# Revit family: Gira_207705
name_source: partatom
category: Electrical Fixtures
revit_build: Autodesk Revit 2017 (Build: 20160225_1515(x64)
units: mm (PartAtom-declared; Revit-internal decimal feet)

## family parameters
Cut with Voids When Loaded = No
Host = Face
Maintain Annotation Orientation = Yes
Part Type = Normal
Room Calculation Point = No
Round Connector Dimension = Use Diameter
Shared = No

## types (1)
- Gira G1 24 V Gira G1 black gl.
    BIM = https://media.live.bim.site
    BIMSITE_PRODUCT_ID = 3473432342bc8b360301786b060e44153b5fdd08
    Bus connection included = No
    Central functional unit for senders/actuators = Yes
    Colour = Black
    Cost = 0 $
    Default Elevation = 1219 mm
    Description = Gira G1 24V G1 GBk Gira G1 24 V,black glass The Gira G1 is a multi-functional room operating device for visualising and operating a variety of building functions. For use in the KNX system and Gira door communication system, or as client. The respective range of functions depends on the firmware used.    When used as a client, the KNX room operating device features are not available. For details on the exact scope of functions, please refer to the Gira online catalogue and the device's technical documentation.,Features: - Operation is via a gesture-capable multi-touch display. - Connection and communication are via LAN or WLAN, depending on the variant. - Integrated speaker. - Integrated microphone with echo compensation.    Potential applications and combinations: - As a multi-functional room operating device, the Gira G1 offers the following functions and function combinations: - KNX room operating device - Home station video - Integrates Internet services or as client for the following systems servers - HomeServer - eNet - X1 - Alarm Connect security system Properties as a KNX room operating device: - Intuitive user interface that can be adapted by the end user. - Switching and dimming (relative and absolute), dimming (incl. Dimming RGB, RGBW, and Tunable White), blind and roller shutter control, value transmitter, and scene auxiliary unit. - Status display, display of date and time, display of indoor and outdoor temperature. - Up to 150 functions (six function folders or rooms with up to 25 functions each). - Up to 125 seven-day timer with 10 switching times each. - Room temperature controller in combination with the temperature sensor module (available as an optional extra), or KNX devices for room temperature measurement, e.g. touch sensor 3 Komfort. - Operating modes: Comfort, standby, night, and frost or heat protection with their own temperature setpoint values (for heating and or cooling). - Operating modes can be adapted individually. - A heating clock as seven-day timer with 28 switching times. - Room temperature controller auxiliary unit for controlling air conditioning systems (fan coil) in conjunction with a KNX gateway for air conditioning systems. Properties as video home station: - Camera changeover: specific selection of connected colour cameras.  - Control of the door opener. - Switching the ringtone on and off. - Ring tone can be selected from a choice of 10 melodies. - Internal calls. Integration of Internet services: - Gira weather service: display of the weather forecast for up to five cities (internet connection required). Gira G1 can also be used as a client for the following systems servers (requires firmware update):: - HomeServer Client - eNet Client - X1 Client - Gira G1 with flush-mounted connection module 24 V WLAN for connecting to a suitable cable (e.g. to the second wire pair of the KNX bus line). - Data communication via WLAN.,Notes : - Suitable for indoor use only. - Recommended mounting height: 150 cm above floor. - Installation is performed on a deep device box (an electronics box is recommended for a LAN connection). - Communication with the KNX installation is exclusively via the KNXnet IP standard. - A KNX IP router must be used to connect the Gira G1 PoE to the KNX installation. Several Gira G1 units can be operated on one KNX IP router. - In order to ensure reliable communication via WLAN, a Gira KNX IP router (firmware version 3 and later) is required to connect the Gira G1 230 V or G1 24 V to the KNX installation. For this purpose the Gira KNX IP router (firmware version 3 and later) is specially equipped with the additional function Reliable data communication". Several Gira G1 units can be operated on one Gira KNX IP router (firmware version 3 and later). - Hardware from index status I08 prepared for KNX Secure (additional firmware update required). - Commissioning in the KNX system from ETS 5.5 or higher. - Can be used as a home station in connection with the DCS-IP gateway. - When planning the system, please observe the technical information on network planning in the device documentation. - The Gira Project Assistant (GPA) is required for firmware updates. The GPA is available free of charge in the Gira download area. - Using the timers requires either an internet connection to a NTP time server or a KNX clock (e.g. Gira weather station Plus 2074 00). - When used as a Gira HomeServer client, the Gira G1's temperature sensor module is not supported. - For dimensioning the power supply, the total power consumption of all connected devices as well as the voltage drop in the supply network must always be considered."
    GTIN = 4010337014287
    HAN = 207705
    HeinzeBIM = https://www.heinze.de
    IR sensor = No
    Integrated DCF77 receiver = No
    Manufacturer = Gira
    Material = Sonstige (*de-DE)
    Material quality = Sonstige (*de-DE)
    Presence button = No
    Status-LED = Yes
    Surface finishing = Not applicable
    Surface protection = Sonstige (*de-DE)
    Temperature controller = Yes
    Transparent = No
    URL = https://www.gira.de
    With anti-theft/dismantling protection = Yes
    With display = Yes
    material_black = Black
    material_white = White

## geometry (parser evidence)
native form markers: Blend x2, Sweep x3
no freeform markers — native parametric forms only
